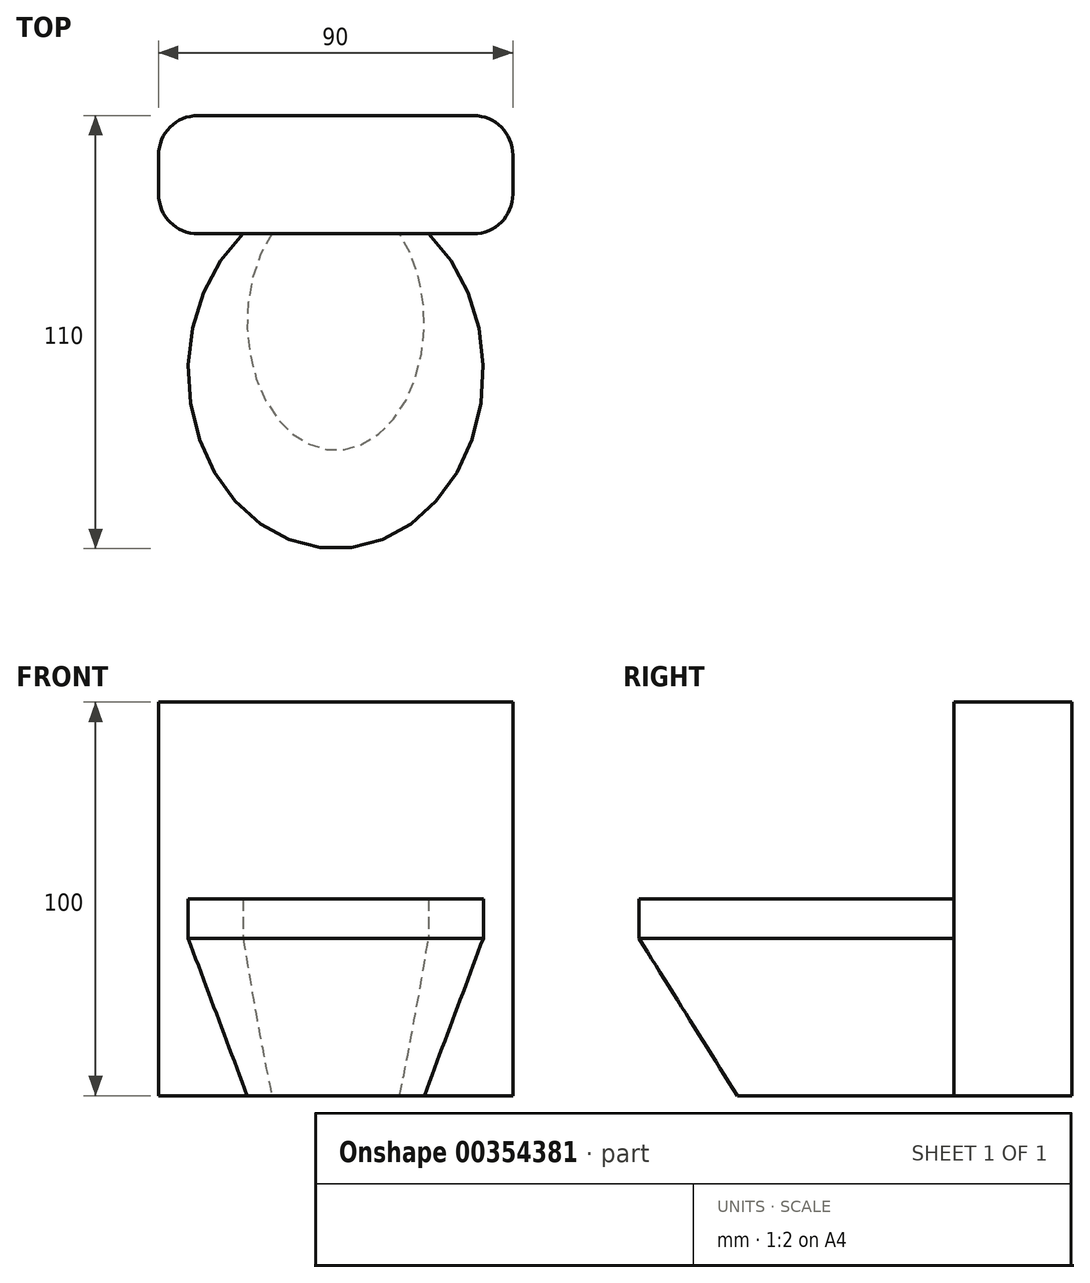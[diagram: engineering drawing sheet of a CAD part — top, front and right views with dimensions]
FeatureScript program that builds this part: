
annotation { "Feature Type Name" : "Feature", "Feature Type Description" : "" }
export const myFeature = defineFeature(function(context is Context, id is Id, definition is map)
    precondition{}
    {
        {
            var Q0;
            Q0=qCreatedBy(makeId("Top.planeOp"),FACE);
            var sketch = newSketch(context, id + "F0", { "sketchPlane" : qUnion([Q0])});
            skEllipse(sketch, "E0", {"center": v(0, 0) * mm, "majorRadius": 45 * mm, "minorRadius": 37.5 * mm, "majorAxis": v(0, 1)});
            skSolve(sketch);
        }
        {
            var Q0;
            Q0=makeQuery(id+"F0.imprint","IMPRINT",FACE,{"disambiguationData":[TD([[makeQuery(id+"F0.imprint","IMPRINT",EDGE,{"derivedFrom":sQuery(id+"F0.wireOp",EDGE,"E0")}),1.0]])]});
            extrude(context, id + "F1", {"entities" : qUnion([Q0]), "depth" : 10 * mm});
        }
        {
            var Q0;
            Q0=qCreatedBy(makeId("Top.planeOp"),FACE);
            cPlane(context, id + "F2", {"entities" : qUnion([Q0]), "cplaneType" : CPlaneType.OFFSET, "offset" : 40 * mm, "oppositeDirection" : true, "width" : 150 * mm, "height" : 150 * mm});
        }
        {
            var Q0;
            Q0=qCreatedBy(id+"F2.planeOp",FACE);
            var sketch = newSketch(context, id + "F3", { "sketchPlane" : qUnion([Q0])});
            skEllipse(sketch, "E1", {"center": v(0, 12.5) * mm, "majorRadius": 32.5 * mm, "minorRadius": 22.5 * mm, "majorAxis": v(0, 1)});
            skSolve(sketch);
        }
        {
            var Q1;
            Q1=makeQuery(id+"F3.imprint","IMPRINT",FACE,{"disambiguationData":[TD([[makeQuery(id+"F3.imprint","IMPRINT",EDGE,{"derivedFrom":sQuery(id+"F3.wireOp",EDGE,"E1")}),1.0]])]});
            var Q2;
            Q2=makeQuery(id+"F1.opExtrude","CAP_FACE",FACE,{"disambiguationData":[OSD([sQuery(id+"F0.wireOp",EDGE,"E0")])],"isStart":true});
            loft(context, id + "F4", {"operationType" : NewBodyOperationType.ADD, "sheetProfilesArray" : [{ "sheetProfileEntities" : qUnion([Q1]) }, { "sheetProfileEntities" : qUnion([Q2]) }]});
        }
        {
            var Q0;
            Q0=qCreatedBy(id+"F2.planeOp",FACE);
            var sketch = newSketch(context, id + "F5", { "sketchPlane" : qUnion([Q0])});
            skLineSegment(sketch, "E2.bottom", {"start": v(-45, 65) * mm, "end": v(45, 65) * mm});
            skLineSegment(sketch, "E2.top", {"start": v(-45, 35) * mm, "end": v(45, 35) * mm});
            skLineSegment(sketch, "E2.left", {"start": v(-45, 65) * mm, "end": v(-45, 35) * mm});
            skLineSegment(sketch, "E2.right", {"start": v(45, 65) * mm, "end": v(45, 35) * mm});
            skPoint(sketch, "E2.middle", {"position": v(0, 50) * mm});
            skSolve(sketch);
        }
        {
            var Q0;
            Q0=makeQuery(id+"F5.imprint","IMPRINT",FACE,{"disambiguationData":[TD([[makeQuery(id+"F5.imprint","IMPRINT",EDGE,{"derivedFrom":sQuery(id+"F5.wireOp",EDGE,"E2.bottom")}),-1.0]])]});
            extrude(context, id + "F6", {"entities" : qUnion([Q0]), "operationType" : NewBodyOperationType.ADD, "depth" : 100 * mm});
        }
        {
            var Q0;
            Q0=makeQuery(id+"F6.opExtrude","SWEPT_EDGE",EDGE,{"disambiguationData":[OSD([sQuery(id+"F5.wireOp",EDGE,"E2.top"),sQuery(id+"F5.wireOp",EDGE,"E2.left")])]});
            var Q1;
            Q1=makeQuery(id+"F6.opExtrude","SWEPT_EDGE",EDGE,{"disambiguationData":[OSD([sQuery(id+"F5.wireOp",EDGE,"E2.bottom"),sQuery(id+"F5.wireOp",EDGE,"E2.left")])]});
            var Q2;
            Q2=makeQuery(id+"F6.opExtrude","SWEPT_EDGE",EDGE,{"disambiguationData":[OSD([sQuery(id+"F5.wireOp",EDGE,"E2.top"),sQuery(id+"F5.wireOp",EDGE,"E2.right")])]});
            var Q3;
            Q3=makeQuery(id+"F6.opExtrude","SWEPT_EDGE",EDGE,{"disambiguationData":[OSD([sQuery(id+"F5.wireOp",EDGE,"E2.bottom"),sQuery(id+"F5.wireOp",EDGE,"E2.right")])]});
            fillet(context, id + "F7", {"entities" : qUnion([Q0, Q1, Q2, Q3]), "radius" : 10 * mm, "tangentPropagation" : true, "allowEdgeOverflow" : false});
        }
    });
